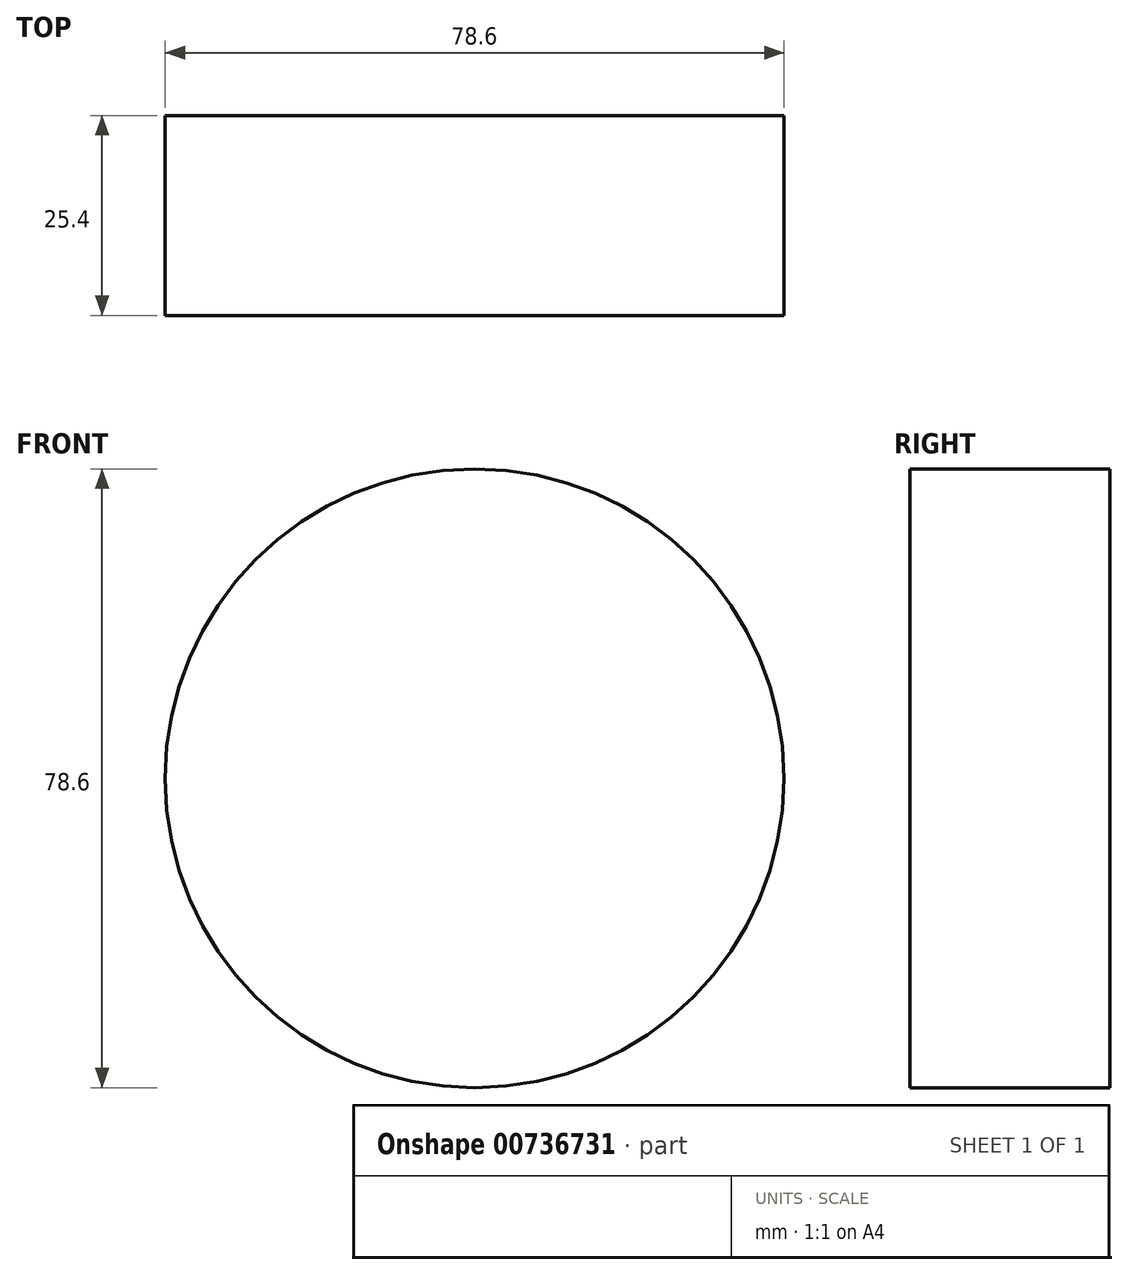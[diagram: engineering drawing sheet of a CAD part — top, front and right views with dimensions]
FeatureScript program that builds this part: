
annotation { "Feature Type Name" : "Feature", "Feature Type Description" : "" }
export const myFeature = defineFeature(function(context is Context, id is Id, definition is map)
    precondition{}
    {
        {
            var Q0;
            Q0=qCreatedBy(makeId("Front.planeOp"),FACE);
            var sketch = newSketch(context, id + "F0", { "sketchPlane" : qUnion([Q0])});
            skCircle(sketch, "E0", {"center": v(0, 0) * mm, "radius": 39.3 * mm});
            skSolve(sketch);
        }
        {
            var Q0;
            Q0 = qSketchRegion(id + "F0", true);
            extrude(context, id + "F1", {"entities" : qUnion([Q0]), "depth" : 25.4 * mm, "offsetDistance" : 25.4 * mm});
        }
    });
